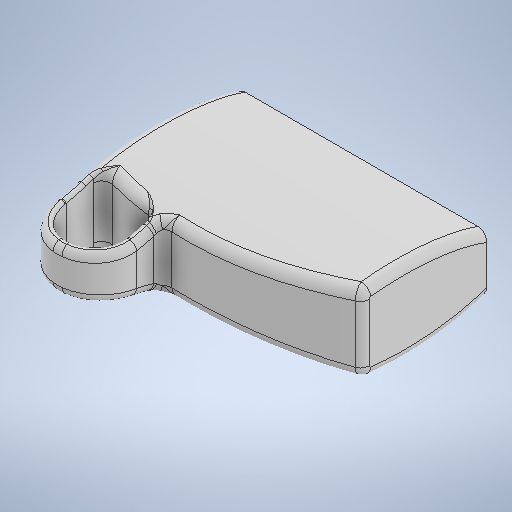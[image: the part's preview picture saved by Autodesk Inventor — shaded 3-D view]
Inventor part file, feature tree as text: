
AUTODESK INVENTOR PART (.ipt)
format: ipt  version: 2025.2 (Build 292293000, 293)  size: 1,095,168 bytes
history: native  units: in
note: dims shown in document units (in); Inventor stores cm internally (conversion verified against a paired STEP export)
features: fillet x6, extrude x5, sketch x4, projected_geometry x3, other x1
ambient origin geometry x8: Origin, YZ Plane, XZ Plane, XY Plane, X Axis, Y Axis, Z Axis, Center Point
bodies: Body1 (feature_tree)
feature tree (19):
  other  "ソリッド1"
  extrude  "押し出し1"  Depth=3.3465in
  sketch  "スケッチ4"
  extrude  "押し出し4"  Depth=0.2756in
  extrude  "押し出し5"  Depth=9.8425in
  extrude  "押し出し6"  Depth=0.8661in TaperAngle=0.0deg
  extrude  "押し出し7"  Depth=0.8268in
  fillet  "フィレット21"  Radius=0.1181in
  fillet  "フィレット22"  Radius=0.1181in
  fillet  "フィレット23"  Radius=1.8504in
  fillet  "フィレット24"  Radius=1.1024in
  fillet  "フィレット25"  Radius=1.5354in
  fillet  "フィレット26"  Radius=3.3465in
  sketch  "スケッチ1"
  projected_geometry  "投影ループ2"
  sketch  "スケッチ5"
  projected_geometry  "投影ループ3"
  sketch  "スケッチ6"
  projected_geometry  "投影ループ4"
